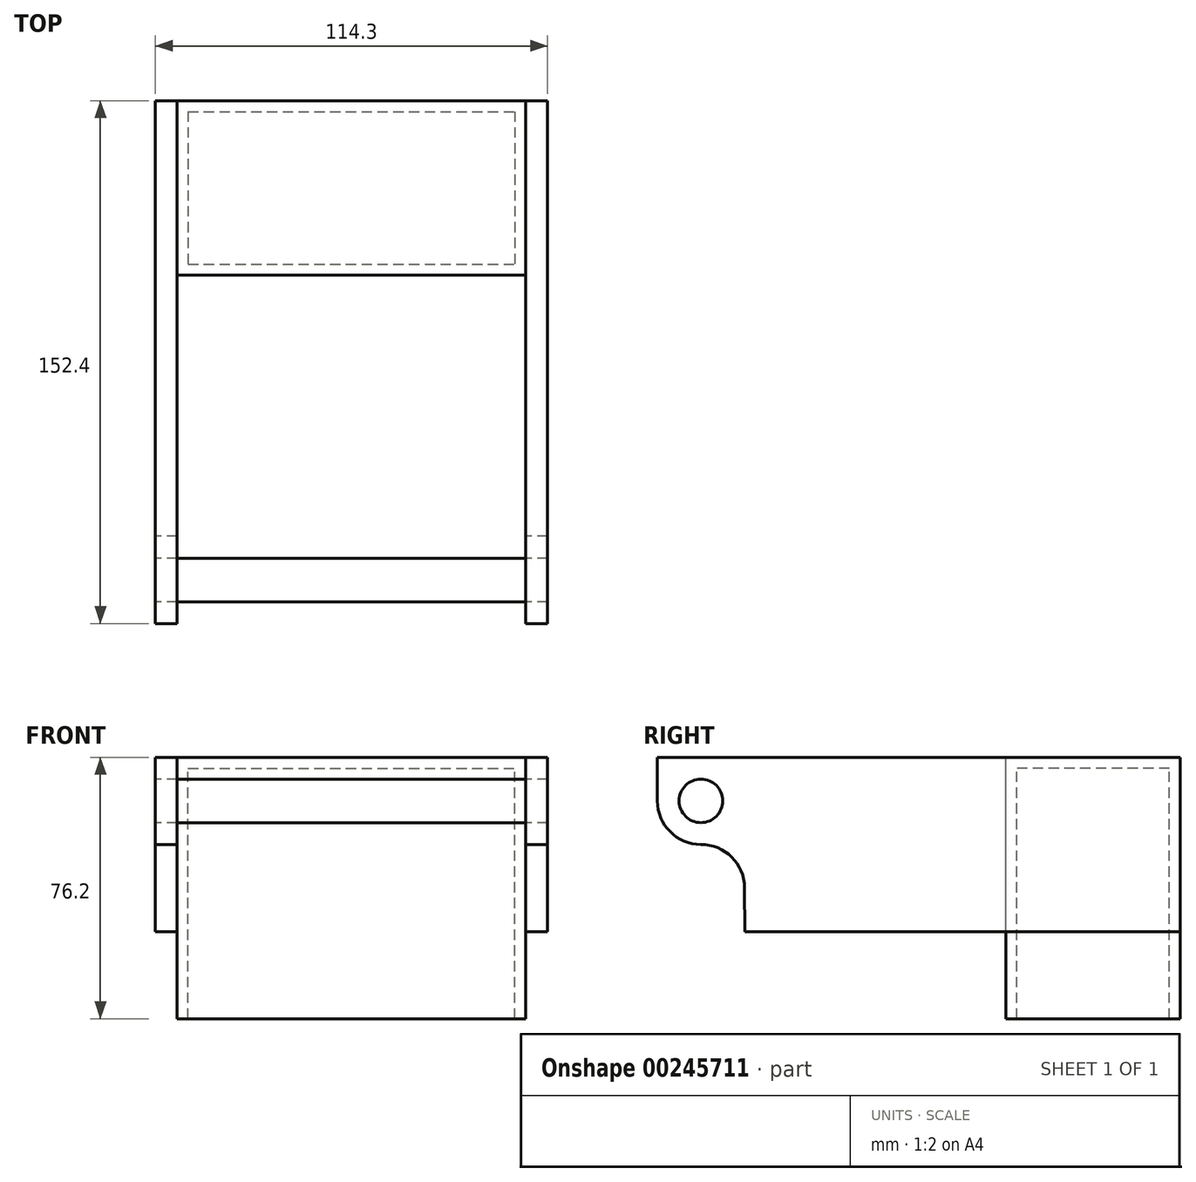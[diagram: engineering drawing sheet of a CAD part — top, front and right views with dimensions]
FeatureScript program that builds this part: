
annotation { "Feature Type Name" : "Feature", "Feature Type Description" : "" }
export const myFeature = defineFeature(function(context is Context, id is Id, definition is map)
    precondition{}
    {
        {
            var Q0;
            Q0=qCreatedBy(makeId("Right.planeOp"),FACE);
            var sketch = newSketch(context, id + "F0", { "sketchPlane" : qUnion([Q0])});
            skLineSegment(sketch, "E0.bottom", {"start": v(-59.59, 14.09) * mm, "end": v(92.81, 14.09) * mm});
            skLineSegment(sketch, "E0.top", {"start": v(-34.1, -36.71) * mm, "end": v(92.81, -36.71) * mm});
            skLineSegment(sketch, "E0.left", {"start": v(-59.59, 14.09) * mm, "end": v(-59.59, 1.39) * mm});
            skLineSegment(sketch, "E0.right", {"start": v(92.81, 14.09) * mm, "end": v(92.81, -36.71) * mm});
            skCircle(sketch, "E1", {"center": v(-46.89, 1.39) * mm, "radius": 6.35 * mm});
            skLineSegment(sketch, "E2", {"start": v(-46.89, -11.31) * mm, "end": v(-46.89, -11.31) * mm});
            skLineSegment(sketch, "E3", {"start": v(-34.19, -23.93) * mm, "end": v(-34.1, -36.71) * mm});
            skPoint(sketch, "E4.visualSharp", {"position": v(-59.59, -11.31) * mm});
            skArc(sketch, "E4.filletArc", {"start": v(-59.59, 1.39) * mm, "mid": v(-55.87, -7.6) * mm, "end": v(-46.89, -11.31) * mm});
            skPoint(sketch, "E5.visualSharp", {"position": v(-34.27, -11.31) * mm});
            skArc(sketch, "E5.filletArc", {"start": v(-34.19, -23.93) * mm, "mid": v(-37.94, -15) * mm, "end": v(-46.89, -11.31) * mm});
            skSolve(sketch);
        }
        {
            var Q0;
            Q0=makeQuery(id+"F0.imprint","IMPRINT",FACE,{"disambiguationData":[TD([[makeQuery(id+"F0.imprint","IMPRINT",EDGE,{"derivedFrom":sQuery(id+"F0.wireOp",EDGE,"E0.bottom")}),-1.0]])]});
            extrude(context, id + "F1", {"entities" : qUnion([Q0]), "depth" : 6.35 * mm});
        }
        {
            var Q0;
            Q0=makeQuery(id+"F0.imprint","IMPRINT",FACE,{"disambiguationData":[TD([[makeQuery(id+"F0.imprint","IMPRINT",EDGE,{"derivedFrom":sQuery(id+"F0.wireOp",EDGE,"E1")}),1.0]])]});
            extrude(context, id + "F2", {"entities" : qUnion([Q0]), "depth" : 114.3 * mm});
        }
        {
            var Q0;
            Q0=makeQuery(id+"F1.opExtrude","SWEPT_FACE",FACE,{"disambiguationData":[OSD([sQuery(id+"F0.wireOp",EDGE,"E0.bottom")])]});
            var sketch = newSketch(context, id + "F3", { "sketchPlane" : qUnion([Q0])});
            skLineSegment(sketch, "E6.bottom", {"start": v(6.35, 92.81) * mm, "end": v(107.95, 92.81) * mm});
            skLineSegment(sketch, "E6.top", {"start": v(6.35, 42.01) * mm, "end": v(107.95, 42.01) * mm});
            skLineSegment(sketch, "E6.left", {"start": v(6.35, 92.81) * mm, "end": v(6.35, 42.01) * mm});
            skLineSegment(sketch, "E6.right", {"start": v(107.95, 92.81) * mm, "end": v(107.95, 42.01) * mm});
            skLineSegment(sketch, "E7.0", {"start": v(9.52, 89.64) * mm, "end": v(104.78, 89.64) * mm});
            skLineSegment(sketch, "E7.1", {"start": v(9.52, 89.64) * mm, "end": v(9.53, 45.19) * mm});
            skLineSegment(sketch, "E7.2", {"start": v(9.52, 45.19) * mm, "end": v(104.78, 45.19) * mm});
            skLineSegment(sketch, "E7.3", {"start": v(104.78, 89.64) * mm, "end": v(104.78, 45.19) * mm});
            skSolve(sketch);
        }
        {
            var Q0;
            Q0=makeQuery(id+"F3.imprint","IMPRINT",FACE,{"disambiguationData":[TD([[makeQuery(id+"F3.imprint","IMPRINT",EDGE,{"derivedFrom":sQuery(id+"F3.wireOp",EDGE,"E6.bottom")}),-1.0]])]});
            extrude(context, id + "F4", {"entities" : qUnion([Q0]), "oppositeDirection" : true, "depth" : 76.2 * mm});
        }
        {
            var Q0;
            Q0=makeQuery(id+"F3.imprint","IMPRINT",FACE,{"disambiguationData":[TD([[makeQuery(id+"F3.imprint","IMPRINT",EDGE,{"derivedFrom":sQuery(id+"F3.wireOp",EDGE,"E7.0")}),-1.0]])]});
            extrude(context, id + "F5", {"entities" : qUnion([Q0]), "operationType" : NewBodyOperationType.ADD, "oppositeDirection" : true, "depth" : 3.17 * mm});
        }
        {
            var Q0;
            Q0=makeQuery(id+"F1.opExtrude","SWEPT_BODY",BODY,{"disambiguationData":[OSD([sQuery(id+"F0.wireOp",EDGE,"E0.bottom"),sQuery(id+"F0.wireOp",EDGE,"E0.top"),sQuery(id+"F0.wireOp",EDGE,"E0.left"),sQuery(id+"F0.wireOp",EDGE,"E0.right"),sQuery(id+"F0.wireOp",EDGE,"E1"),sQuery(id+"F0.wireOp",EDGE,"E2"),sQuery(id+"F0.wireOp",EDGE,"E3"),sQuery(id+"F0.wireOp",EDGE,"E4.filletArc"),sQuery(id+"F0.wireOp",EDGE,"E5.filletArc")])]});
            var Q1;
            Q1=qCreatedBy(makeId("Right.planeOp"),FACE);
            transform(context, id + "F6", {"entities" : qUnion([Q0]), "transformType" : TransformType.TRANSLATION_DISTANCE, "transformDirection" : qUnion([Q1]), "distance" : 107.95 * mm, "makeCopy" : true});
        }
    });
